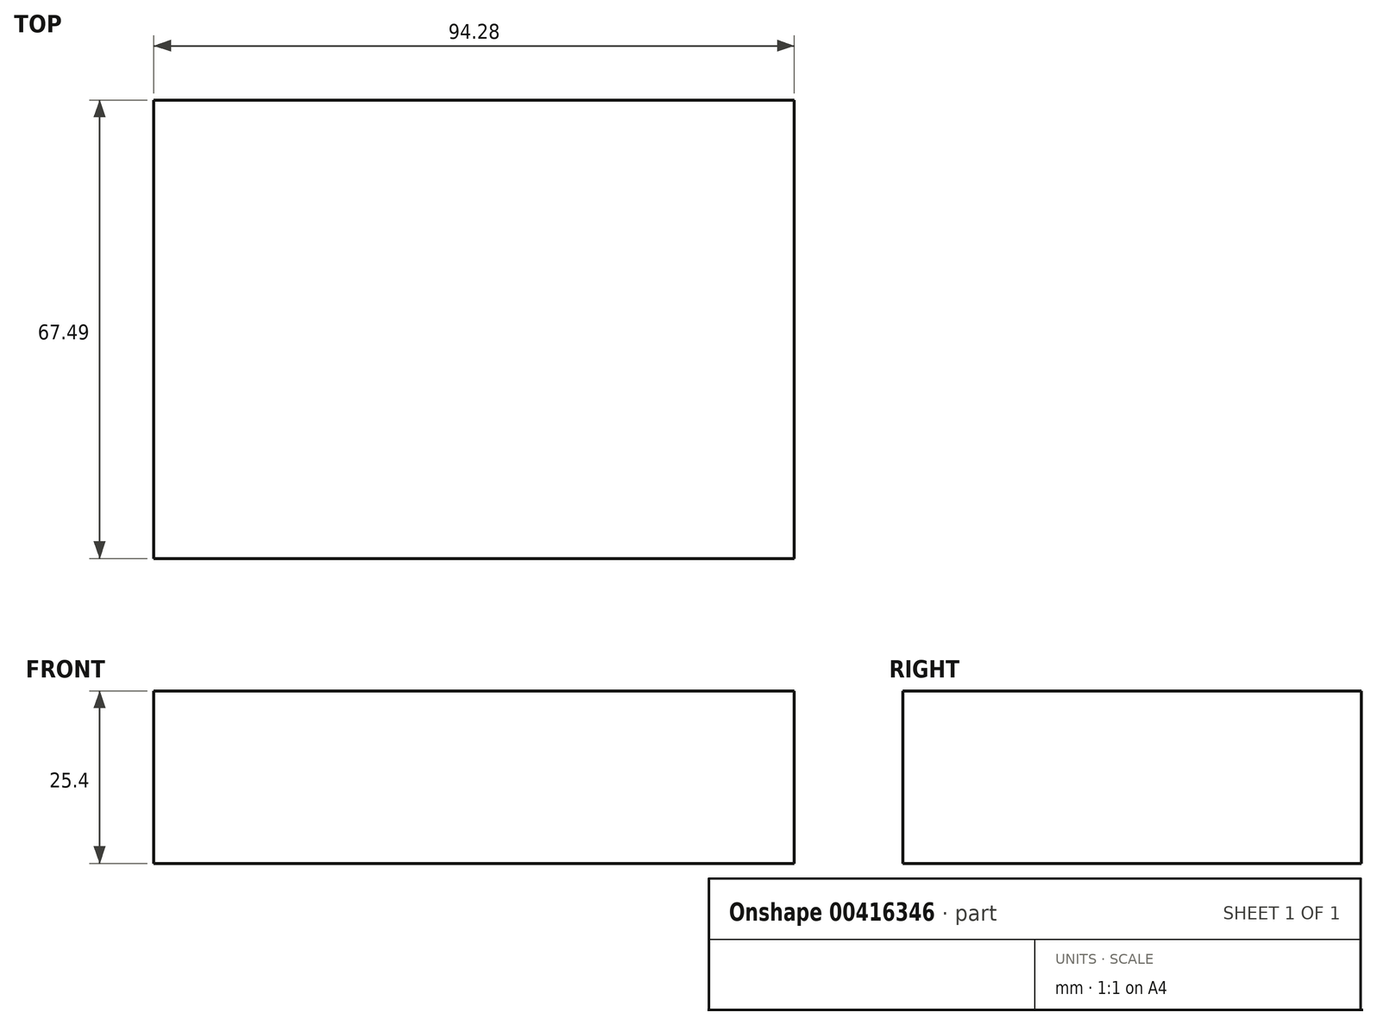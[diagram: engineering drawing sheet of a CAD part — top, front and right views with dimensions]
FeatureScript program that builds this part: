
annotation { "Feature Type Name" : "Feature", "Feature Type Description" : "" }
export const myFeature = defineFeature(function(context is Context, id is Id, definition is map)
    precondition{}
    {
        {
            var Q0;
            Q0=qCreatedBy(makeId("Top.planeOp"),FACE);
            var sketch = newSketch(context, id + "F0", { "sketchPlane" : qUnion([Q0])});
            skLineSegment(sketch, "E0.bottom", {"start": v(-56.45, 28.37) * mm, "end": v(37.83, 28.37) * mm});
            skLineSegment(sketch, "E0.top", {"start": v(-56.45, -39.12) * mm, "end": v(37.83, -39.12) * mm});
            skLineSegment(sketch, "E0.left", {"start": v(-56.45, 28.37) * mm, "end": v(-56.45, -39.12) * mm});
            skLineSegment(sketch, "E0.right", {"start": v(37.83, 28.37) * mm, "end": v(37.83, -39.12) * mm});
            skSolve(sketch);
        }
        {
            var Q0;
            Q0 = qSketchRegion(id + "F0", true);
            var Q1;
            Q1=makeQuery(id+"F0.imprint","IMPRINT",FACE,{"disambiguationData":[TD([[makeQuery(id+"F0.imprint","IMPRINT",EDGE,{"derivedFrom":sQuery(id+"F0.wireOp",EDGE,"E0.bottom")}),-1.0]])]});
            extrude(context, id + "F1", {"entities" : qUnion([Q0, Q1]), "depth" : 25.4 * mm});
        }
    });
